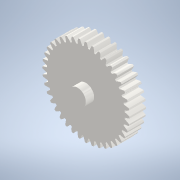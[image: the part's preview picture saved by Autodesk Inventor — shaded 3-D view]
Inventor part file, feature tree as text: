
AUTODESK INVENTOR PART (.ipt)
format: ipt  version: 2020 (Build 240168000, 168)  size: 352,256 bytes
history: native  units: mm (DEFAULTED — no unit token found)
features: sketch x6, other x5, extrude x5, plane x4
ambient origin geometry x8: Origin, YZ Plane, XZ Plane, XY Plane, X Axis, Y Axis, Z Axis, Center Point
bodies: Solid1 (feature_tree)
feature tree (20):
  other  "Annotations"
  extrude  "Extrusion1"  Depth=20.0mm TaperAngle=0.0deg
  plane  "Work Plane2"
  plane  "Work Plane8"
  plane  "Work Plane9"
  other  "Spur Gear"
  extrude  "Extrusion2"  Depth=10.0mm TaperAngle=0.0deg
  plane  "Work Plane13"
  extrude  "Extrusion3"  Depth=0.785398mm TaperAngle=0.0deg
  extrude  "Extrusion4"  TaperAngle=0.0deg  [1 undecoded]
  extrude  "Extrusion5"  Depth=62.5mm
  sketch  "Sketch1"  dims[d0=105.0mm d1=20.0mm d2=0.0mm]
  sketch  "Sketch2"  dims[d3=100.0mm d4=10.0mm d5=0.0mm]
  other  "Srf1"
  sketch  "Sketch3"  dims[d16=62.5mm d17=0.0mm d34=0.785398mm]
  sketch  "Sketch5"  dims[d39=0.0mm d41=0.0mm]
  sketch  "Sketch6"  dims[d43=62.5mm d46=62.5mm]
  sketch  "Sketch7"  dims[d47=0.0mm d48=0.0mm d49=20.0mm d50=10.0mm d51=0.0mm d53=10.0mm d54=3.0mm d55=25.0mm d56=12.0mm d57=0.0mm d58=5.2mm d59=0.0mm d60=0.0mm d61=2.5mm d63=5.5mm d64=0.0mm d65=5.0mm d66=8.0mm d67=0.0mm d52=2.036157mm]
  other  "Pitch Diameter"
  other  "Linear Dimension 1"
note: 1 required parameter value undecoded (feature->parameter linkage not recoverable at this tier; creation-order binding heuristic only, values carry confidence <= 0.55)
